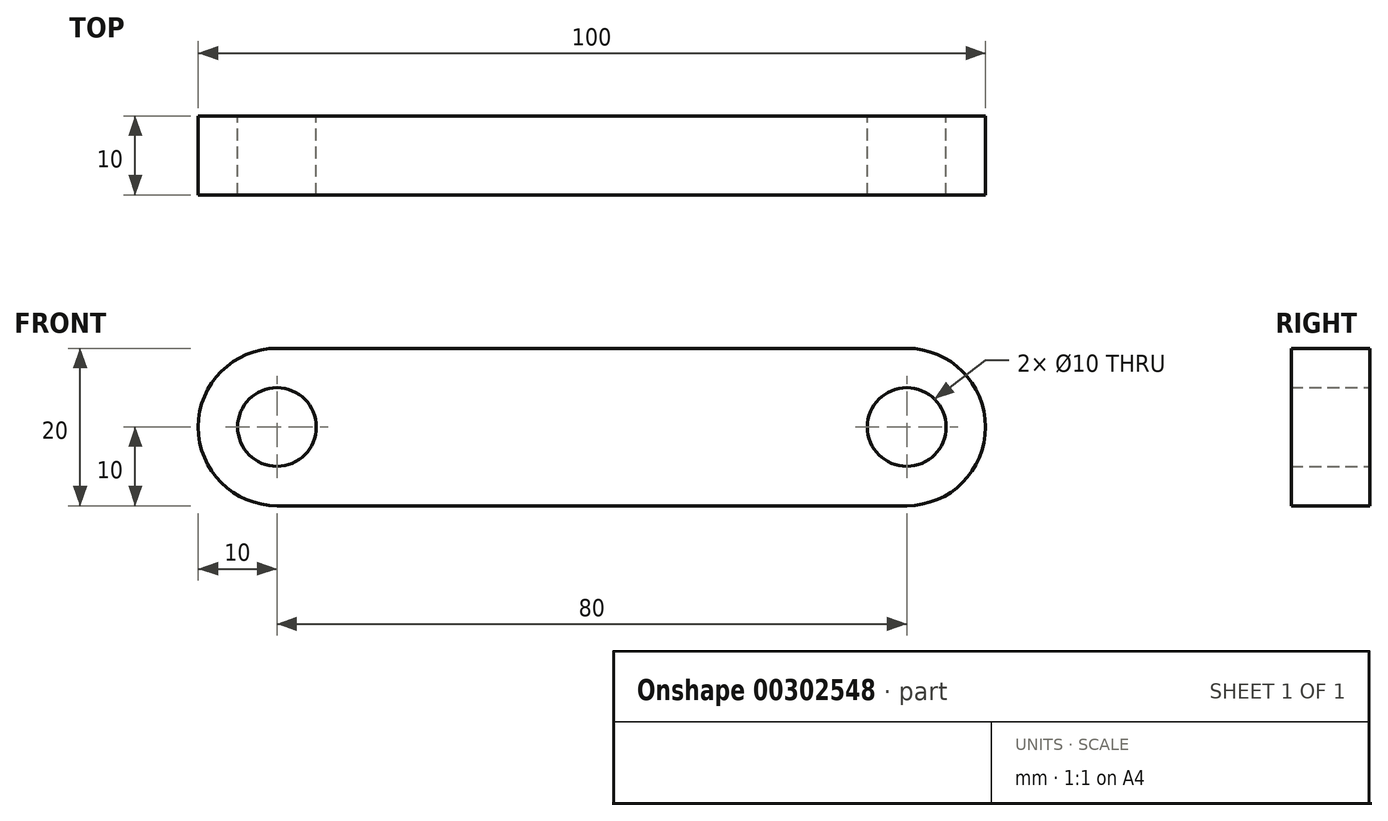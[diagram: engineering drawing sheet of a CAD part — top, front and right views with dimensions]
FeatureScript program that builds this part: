
annotation { "Feature Type Name" : "Feature", "Feature Type Description" : "" }
export const myFeature = defineFeature(function(context is Context, id is Id, definition is map)
    precondition{}
    {
        {
            var Q0;
            Q0=qCreatedBy(makeId("Front.planeOp"),FACE);
            var sketch = newSketch(context, id + "F0", { "sketchPlane" : qUnion([Q0])});
            skLineSegment(sketch, "E0", {"start": v(0, 10) * mm, "end": v(80, 10) * mm});
            skCircle(sketch, "E1", {"center": v(80, 0) * mm, "radius": 5 * mm});
            skCircle(sketch, "E2", {"center": v(0, 0) * mm, "radius": 5 * mm});
            skArc(sketch, "E3", {"start": v(80, -10) * mm, "mid": v(90, 0) * mm, "end": v(80, 10) * mm});
            skLineSegment(sketch, "E4", {"start": v(80, -10) * mm, "end": v(0, -10) * mm});
            skArc(sketch, "E5", {"start": v(0, 10) * mm, "mid": v(-10, 0) * mm, "end": v(0, -10) * mm});
            skSolve(sketch);
        }
        {
            var Q0;
            Q0 = qSketchRegion(id + "F0", true);
            extrude(context, id + "F1", {"entities" : qUnion([Q0]), "depth" : 10 * mm});
        }
    });
